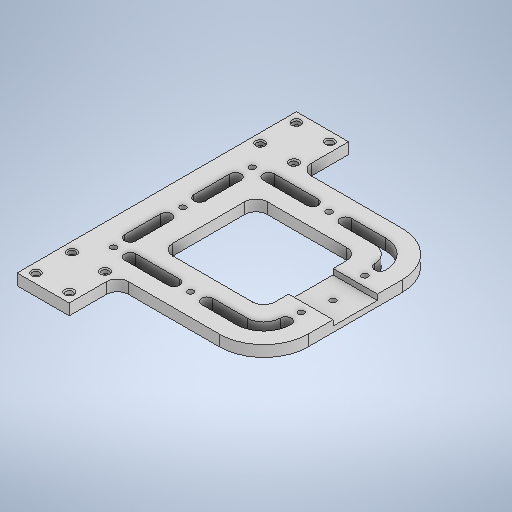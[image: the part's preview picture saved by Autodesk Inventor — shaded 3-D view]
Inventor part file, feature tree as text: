
AUTODESK INVENTOR PART (.ipt)
format: ipt  version: 2025.2 (Build 292293000, 293)  size: 446,976 bytes
history: native  units: mm
features: sketch x7, extrude x6, fillet x2
ambient origin geometry x8: Origin, YZ Plane, XZ Plane, XY Plane, X Axis, Y Axis, Z Axis, Center Point
bodies: Solid1 (feature_tree)
feature tree (15):
  extrude  "Extrusion1"  Depth=252.0mm
  extrude  "Extrusion2"  Depth=40.0mm
  fillet  "Fillet1"  Radius=92.0mm
  extrude  "Extrusion3"  Depth=40.0mm
  extrude  "Extrusion4"  Depth=3.6mm
  fillet  "Fillet2"  Radius=3.6mm
  extrude  "Extrusion5"  Depth=10.0mm
  sketch  "Sketch6"  dims[d19=6.5mm d20=6.5mm]
  extrude  "Extrusion6"  Depth=6.5mm
  sketch  "Sketch1"  dims[d0=47.0mm d1=252.0mm]
  sketch  "Sketch2"  dims[d8=92.0mm d9=40.0mm d10=92.0mm]
  sketch  "Sketch3"  dims[d11=40.0mm d12=3.6mm]
  sketch  "Sketch4"  dims[d13=3.6mm d14=3.6mm d15=3.6mm]
  sketch  "Sketch5"  dims[d16=10.0mm d17=0.0mm d18=6.5mm]
  sketch  "Sketch7"  dims[d21=6.5mm d22=6.5mm d23=6.5mm d24=6.5mm d25=6.5mm d26=4.0mm d27=0.0mm d28=1.0mm d31=40.0mm d32=0.0mm d33=40.0mm d34=5.0mm d35=5.5mm d36=5.5mm d37=5.5mm d38=5.5mm d39=5.5mm d40=5.5mm d41=0.0mm d42=0.0mm d43=10.0mm d44=10.0mm d45=10.0mm d46=10.0mm d47=10.0mm d48=10.0mm d49=10.0mm d50=10.0mm d51=0.0mm d52=5.5mm d53=5.5mm d54=10.0mm d55=0.0mm]
